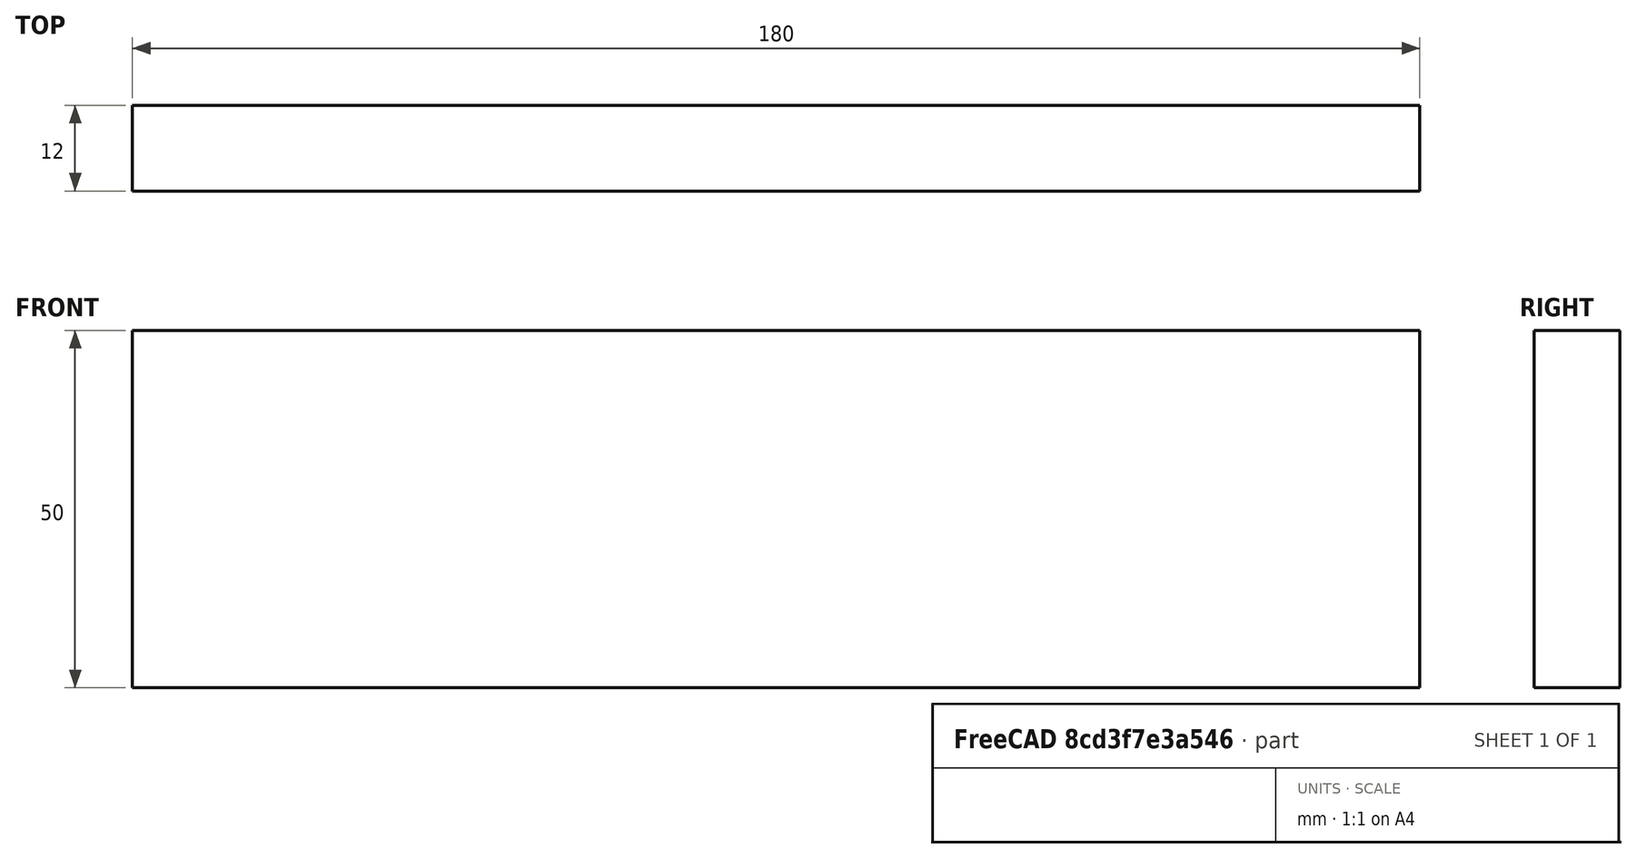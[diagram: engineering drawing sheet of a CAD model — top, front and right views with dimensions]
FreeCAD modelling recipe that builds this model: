
FCSTD DOCUMENT  (FreeCAD 0.15R4671 (Git))
Label: Flat Bar 180x12 EN10058 S235JR
License: All rights reserved
LicenseURL: http://en.wikipedia.org/wiki/All_rights_reserved
objects: Sketcher::SketchObject×1, Part::Extrusion×1
note: 2 computed .brp shape members not serialized (recipe doc carries the construction recipe); baked Part::Feature solids carry a one-line shape summary decoded from their .brp

FEATURE [Sketcher::SketchObject] Sketch
  sketch-geometry (4):
    g0: LineSegment StartX=-90 StartY=-6 StartZ=0 EndX=90 EndY=-6 EndZ=0
    g1: LineSegment StartX=90 StartY=-6 StartZ=0 EndX=90 EndY=6 EndZ=0
    g2: LineSegment StartX=90 StartY=6 StartZ=0 EndX=-90 EndY=6 EndZ=0
    g3: LineSegment StartX=-90 StartY=6 StartZ=0 EndX=-90 EndY=-6 EndZ=0
  constraints (12):
    c: Coincident(g0,g1)
    c: Coincident(g1,g2)
    c: Coincident(g2,g3)
    c: Coincident(g3,g0)
    c: Horizontal(g0)
    c: Horizontal(g2)
    c: Vertical(g1)
    c: Vertical(g3)
    c: Symmetric(g1,g2,g-2)
    c: Symmetric(g0,g1,g-1)
    c: DistanceY(g1) = 12
    c: DistanceX(g0) = 180
FEATURE [Part::Extrusion] Extrude  label="Flat Bar 180x12 EN10058 S235JR"
  Base = -> Sketch
  Dir = (0,0,50)
  Solid = true
